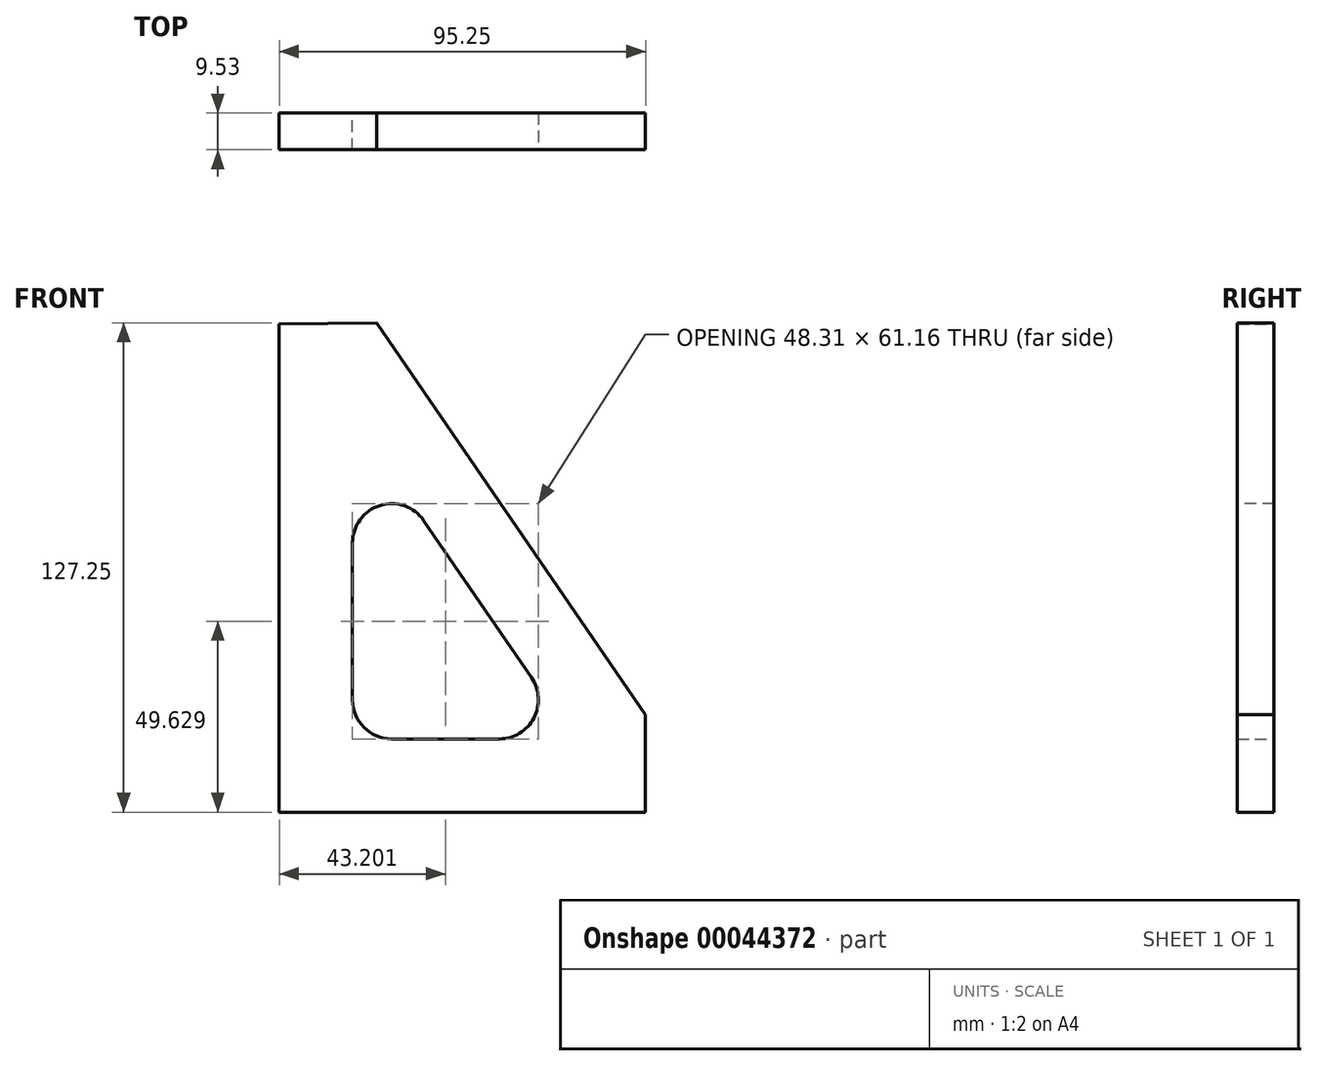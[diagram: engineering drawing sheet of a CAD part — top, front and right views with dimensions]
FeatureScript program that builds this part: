
annotation { "Feature Type Name" : "Feature", "Feature Type Description" : "" }
export const myFeature = defineFeature(function(context is Context, id is Id, definition is map)
    precondition{}
    {
        {
            var Q0;
            Q0=qCreatedBy(makeId("Front.planeOp"),FACE);
            var sketch = newSketch(context, id + "F0", { "sketchPlane" : qUnion([Q0])});
            skLineSegment(sketch, "E0", {"start": v(-57.34, 53.16) * mm, "end": v(-57.34, -73.84) * mm});
            skLineSegment(sketch, "E1", {"start": v(-57.34, -73.84) * mm, "end": v(37.9, -73.84) * mm});
            skLineSegment(sketch, "E2", {"start": v(37.9, -73.84) * mm, "end": v(37.9, -48.44) * mm});
            skLineSegment(sketch, "E3", {"start": v(37.9, -48.44) * mm, "end": v(-31.95, 53.41) * mm});
            skLineSegment(sketch, "E4", {"start": v(-31.95, 53.41) * mm, "end": v(-57.34, 53.16) * mm});
            skLineSegment(sketch, "E5", {"start": v(-38.3, 28.99) * mm, "end": v(-38.3, -54.8) * mm});
            skLineSegment(sketch, "E6", {"start": v(-38.3, -54.8) * mm, "end": v(19.16, -54.8) * mm});
            skLineSegment(sketch, "E7", {"start": v(19.16, -54.8) * mm, "end": v(-38.3, 28.99) * mm});
            skSolve(sketch);
        }
        {
            var Q0;
            Q0 = qSketchRegion(id + "F0", true);
            extrude(context, id + "F1", {"entities" : qUnion([Q0]), "depth" : 9.52 * mm});
        }
        {
            var Q0;
            Q0=makeQuery(id+"F1.opExtrude","SWEPT_EDGE",EDGE,{"disambiguationData":[OSD([sQuery(id+"F0.wireOp",EDGE,"E5"),sQuery(id+"F0.wireOp",EDGE,"E6")])]});
            var Q1;
            Q1=makeQuery(id+"F1.opExtrude","SWEPT_EDGE",EDGE,{"disambiguationData":[OSD([sQuery(id+"F0.wireOp",EDGE,"E6"),sQuery(id+"F0.wireOp",EDGE,"E7")])]});
            var Q2;
            Q2=makeQuery(id+"F1.opExtrude","SWEPT_EDGE",EDGE,{"disambiguationData":[OSD([sQuery(id+"F0.wireOp",EDGE,"E5"),sQuery(id+"F0.wireOp",EDGE,"E7")])]});
            fillet(context, id + "F2", {"entities" : qUnion([Q0, Q1, Q2]), "radius" : 10.16 * mm, "tangentPropagation" : true, "allowEdgeOverflow" : false});
        }
    });
